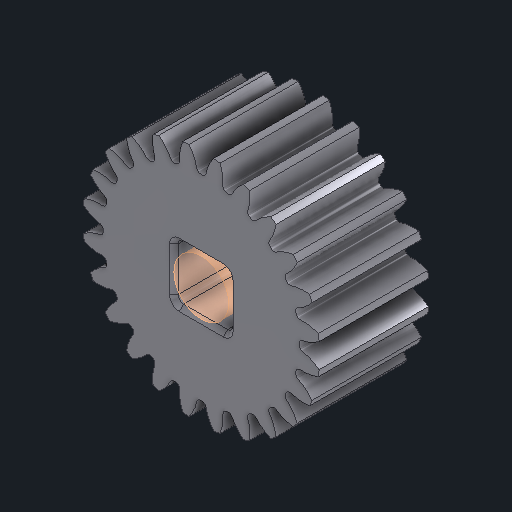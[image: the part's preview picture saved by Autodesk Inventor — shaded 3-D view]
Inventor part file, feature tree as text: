
AUTODESK INVENTOR PART (.ipt)
format: ipt  version: 2025 (Build 290162000, 162)  size: 467,456 bytes
history: native  units: in
note: dims shown in document units (in); Inventor stores cm internally (conversion verified against a paired STEP export)
features: other x5, sketch x1
ambient origin geometry x8: Origin, YZ Plane, XZ Plane, XY Plane, X Axis, Y Axis, Z Axis, Center Point
bodies: Solid1 (feature_tree)
feature tree (6):
  other  "HS 24T Gear, No Insert.ipt"
  other  "Solid1::HS 24T Gear, No Insert.ipt"
  other  "TaggingFeature1"
  sketch  "Sketch1"  dims[d0=0.3937in]
  other  "Srf1"
  other  "Srf1::Derived"
